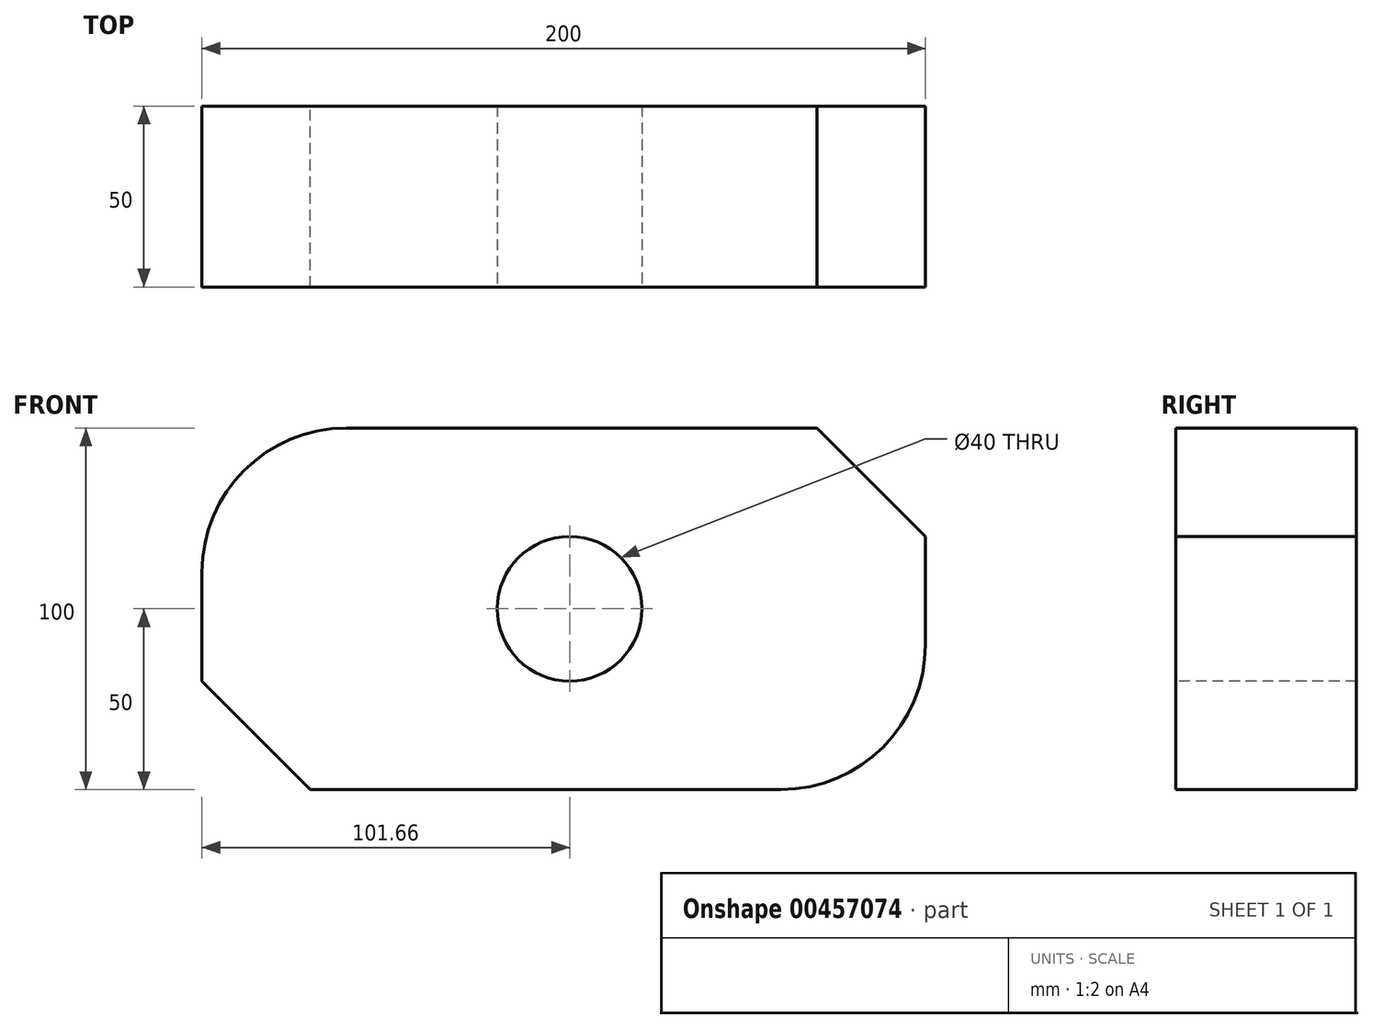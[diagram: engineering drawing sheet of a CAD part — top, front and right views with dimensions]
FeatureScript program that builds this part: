
annotation { "Feature Type Name" : "Feature", "Feature Type Description" : "" }
export const myFeature = defineFeature(function(context is Context, id is Id, definition is map)
    precondition{}
    {
        {
            var Q0;
            Q0=qCreatedBy(makeId("Front.planeOp"),FACE);
            var sketch = newSketch(context, id + "F0", { "sketchPlane" : qUnion([Q0])});
            skLineSegment(sketch, "E0.bottom", {"start": v(100, 50) * mm, "end": v(-100, 50) * mm});
            skLineSegment(sketch, "E0.top", {"start": v(100, -50) * mm, "end": v(-100, -50) * mm});
            skLineSegment(sketch, "E0.left", {"start": v(100, 50) * mm, "end": v(100, -50) * mm});
            skLineSegment(sketch, "E0.right", {"start": v(-100, 50) * mm, "end": v(-100, -50) * mm});
            skPoint(sketch, "E0.middle", {"position": v(0, 0) * mm});
            skSolve(sketch);
        }
        {
            var Q0;
            Q0=makeQuery(id+"F0.imprint","IMPRINT",FACE,{"disambiguationData":[TD([[makeQuery(id+"F0.imprint","IMPRINT",EDGE,{"derivedFrom":sQuery(id+"F0.wireOp",EDGE,"E0.bottom")}),1.0]])]});
            extrude(context, id + "F1", {"entities" : qUnion([Q0]), "depth" : 50 * mm});
        }
        {
            var Q0;
            Q0=makeQuery(id+"F1.opExtrude","SWEPT_EDGE",EDGE,{"disambiguationData":[OSD([sQuery(id+"F0.wireOp",EDGE,"E0.top"),sQuery(id+"F0.wireOp",EDGE,"E0.right")])]});
            var Q1;
            Q1=makeQuery(id+"F1.opExtrude","SWEPT_EDGE",EDGE,{"disambiguationData":[OSD([sQuery(id+"F0.wireOp",EDGE,"E0.bottom"),sQuery(id+"F0.wireOp",EDGE,"E0.left")])]});
            chamfer(context, id + "F2", {"entities" : qUnion([Q0, Q1]), "width" : 30 * mm, "tangentPropagation" : true});
        }
        {
            var Q0;
            Q0=makeQuery(id+"F1.opExtrude","SWEPT_EDGE",EDGE,{"disambiguationData":[OSD([sQuery(id+"F0.wireOp",EDGE,"E0.bottom"),sQuery(id+"F0.wireOp",EDGE,"E0.right")])]});
            var Q1;
            Q1=makeQuery(id+"F1.opExtrude","SWEPT_EDGE",EDGE,{"disambiguationData":[OSD([sQuery(id+"F0.wireOp",EDGE,"E0.top"),sQuery(id+"F0.wireOp",EDGE,"E0.left")])]});
            fillet(context, id + "F3", {"entities" : qUnion([Q0, Q1]), "radius" : 40 * mm, "tangentPropagation" : true, "allowEdgeOverflow" : false});
        }
        {
            var Q0;
            Q0=makeQuery(id+"F1.opExtrude","CAP_FACE",FACE,{"disambiguationData":[OSD([sQuery(id+"F0.wireOp",EDGE,"E0.bottom"),sQuery(id+"F0.wireOp",EDGE,"E0.top"),sQuery(id+"F0.wireOp",EDGE,"E0.left"),sQuery(id+"F0.wireOp",EDGE,"E0.right")])],"isStart":false});
            var sketch = newSketch(context, id + "F4", { "sketchPlane" : qUnion([Q0])});
            skCircle(sketch, "E1", {"center": v(1.66, 0) * mm, "radius": 20 * mm});
            skSolve(sketch);
        }
        {
            var Q0;
            Q0=makeQuery(id+"F4.imprint","IMPRINT",FACE,{"disambiguationData":[TD([[makeQuery(id+"F4.imprint","IMPRINT",EDGE,{"derivedFrom":sQuery(id+"F4.wireOp",EDGE,"E1")}),1.0]])]});
            extrude(context, id + "F5", {"entities" : qUnion([Q0]), "operationType" : NewBodyOperationType.REMOVE, "endBound" : BoundingType.THROUGH_ALL, "oppositeDirection" : true, "depth" : 25 * mm});
        }
    });
